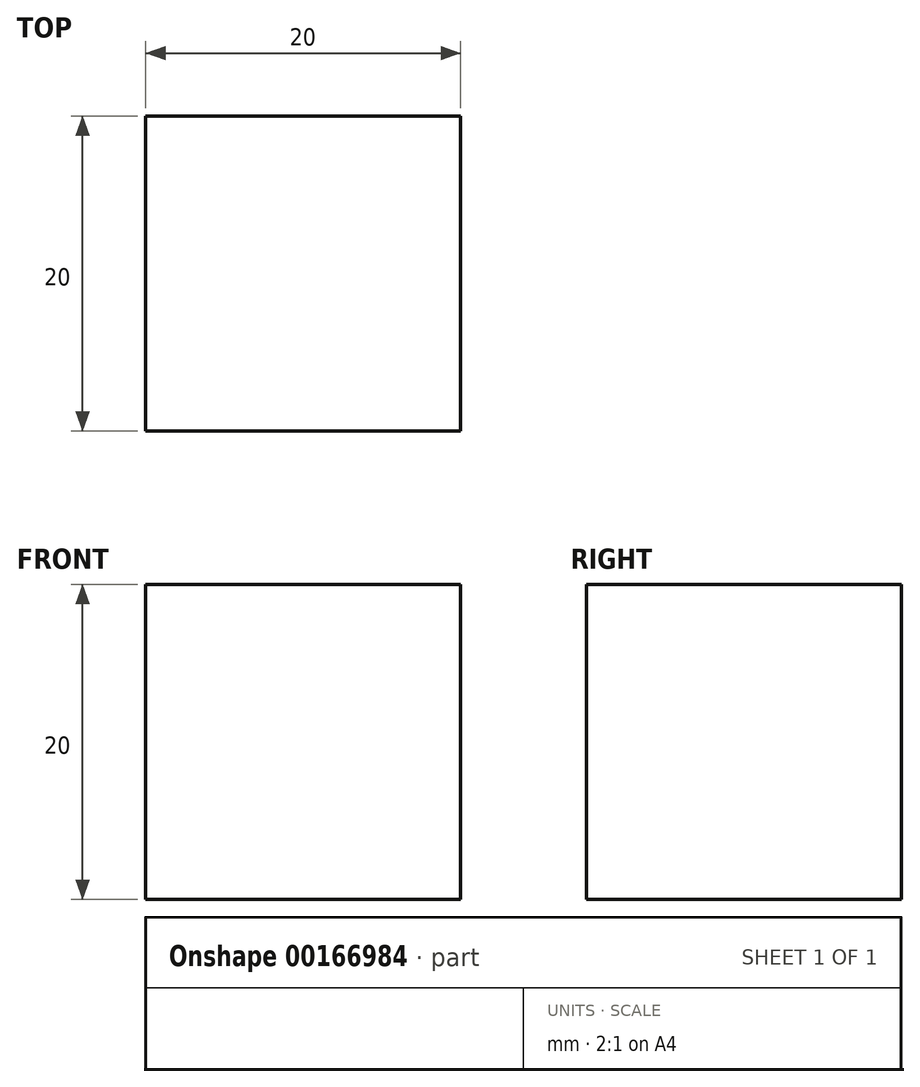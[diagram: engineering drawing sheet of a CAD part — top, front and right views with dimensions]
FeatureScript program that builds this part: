
annotation { "Feature Type Name" : "Feature", "Feature Type Description" : "" }
export const myFeature = defineFeature(function(context is Context, id is Id, definition is map)
    precondition{}
    {
        {
            var Q0;
            Q0=qCreatedBy(makeId("Front.planeOp"),FACE);
            var sketch = newSketch(context, id + "F0", { "sketchPlane" : qUnion([Q0])});
            skLineSegment(sketch, "E0.bottom", {"start": v(10, -10) * mm, "end": v(-10, -10) * mm});
            skLineSegment(sketch, "E0.top", {"start": v(10, 10) * mm, "end": v(-10, 10) * mm});
            skLineSegment(sketch, "E0.left", {"start": v(10, -10) * mm, "end": v(10, 10) * mm});
            skLineSegment(sketch, "E0.right", {"start": v(-10, -10) * mm, "end": v(-10, 10) * mm});
            skPoint(sketch, "E0.middle", {"position": v(0, 0) * mm});
            skSolve(sketch);
        }
        {
            var Q0;
            Q0=makeQuery(id+"F0.imprint","IMPRINT",FACE,{"disambiguationData":[TD([[makeQuery(id+"F0.imprint","IMPRINT",EDGE,{"derivedFrom":sQuery(id+"F0.wireOp",EDGE,"E0.bottom")}),-1.0]])]});
            extrude(context, id + "F1", {"entities" : qUnion([Q0]), "depth" : 20 * mm});
        }
    });
